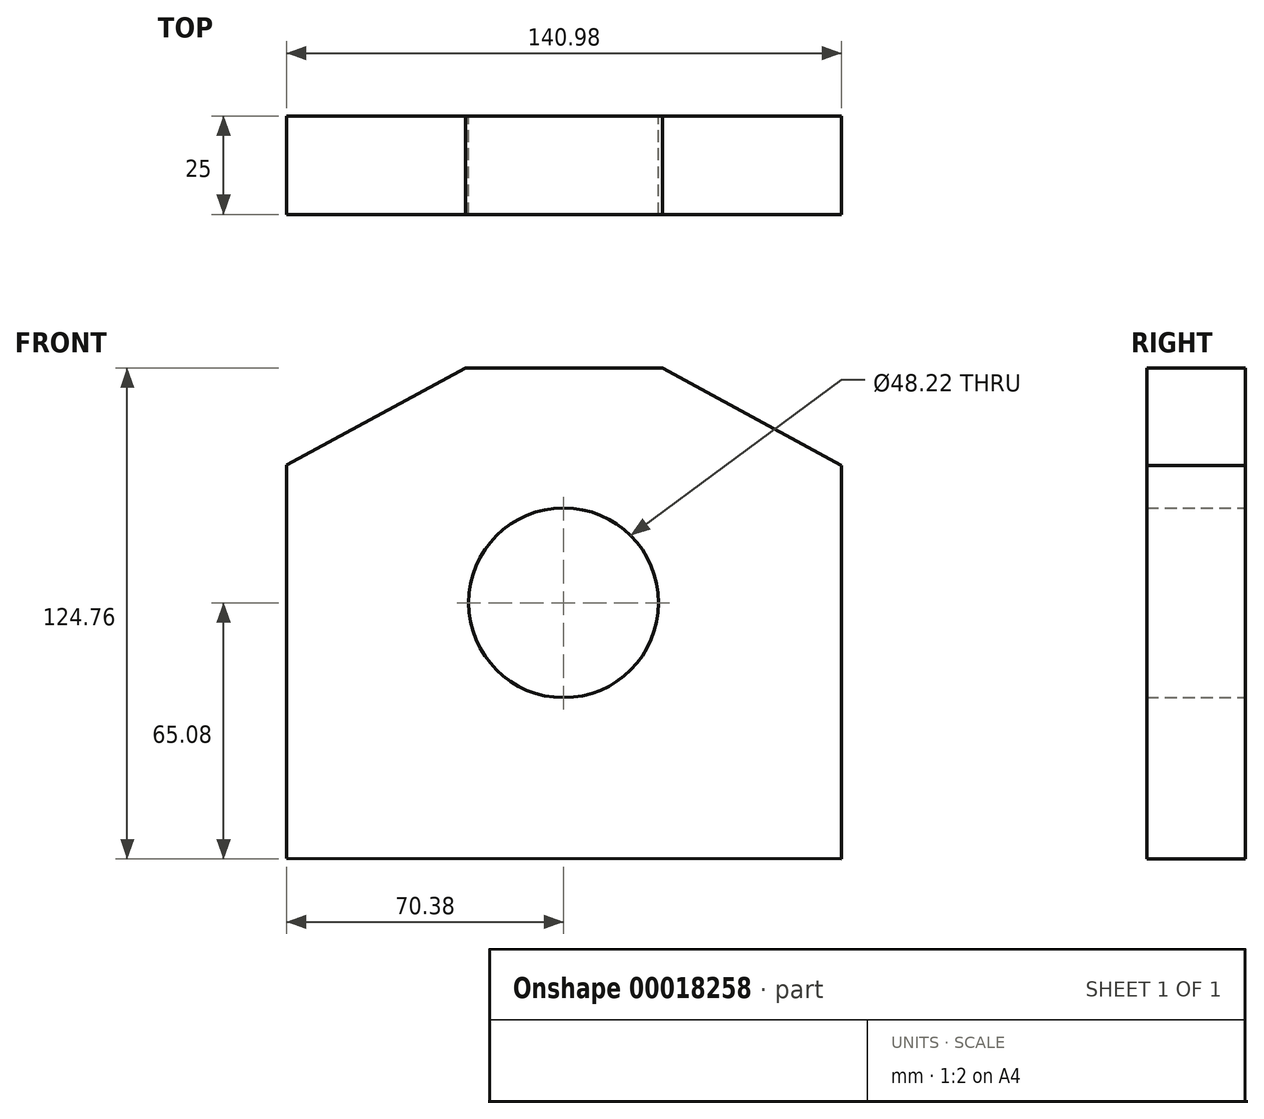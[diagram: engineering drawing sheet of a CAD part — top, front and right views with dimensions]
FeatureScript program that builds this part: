
annotation { "Feature Type Name" : "Feature", "Feature Type Description" : "" }
export const myFeature = defineFeature(function(context is Context, id is Id, definition is map)
    precondition{}
    {
        {
            var Q0;
            Q0=qCreatedBy(makeId("Front.planeOp"),FACE);
            var sketch = newSketch(context, id + "F0", { "sketchPlane" : qUnion([Q0])});
            skCircle(sketch, "E0", {"center": v(0, 0) * mm, "radius": 24.1 * mm});
            skLineSegment(sketch, "E1", {"start": v(-70.38, -64.97) * mm, "end": v(-70.38, 35.03) * mm});
            skLineSegment(sketch, "E2", {"start": v(-70.38, 35.03) * mm, "end": v(-24.86, 59.68) * mm});
            skLineSegment(sketch, "E3", {"start": v(-24.86, 59.68) * mm, "end": v(25.14, 59.68) * mm});
            skLineSegment(sketch, "E4", {"start": v(25.14, 59.68) * mm, "end": v(70.6, 34.92) * mm});
            skLineSegment(sketch, "E5", {"start": v(70.6, 34.92) * mm, "end": v(70.6, -65.08) * mm});
            skLineSegment(sketch, "E6", {"start": v(70.6, -65.08) * mm, "end": v(-70.38, -64.97) * mm});
            skSolve(sketch);
        }
        {
            var Q0;
            Q0=makeQuery(id+"F0.imprint","IMPRINT",FACE,{"disambiguationData":[TD([[makeQuery(id+"F0.imprint","IMPRINT",EDGE,{"derivedFrom":sQuery(id+"F0.wireOp",EDGE,"E0")}),-1.0]])]});
            extrude(context, id + "F1", {"entities" : qUnion([Q0]), "depth" : 25 * mm});
        }
    });
